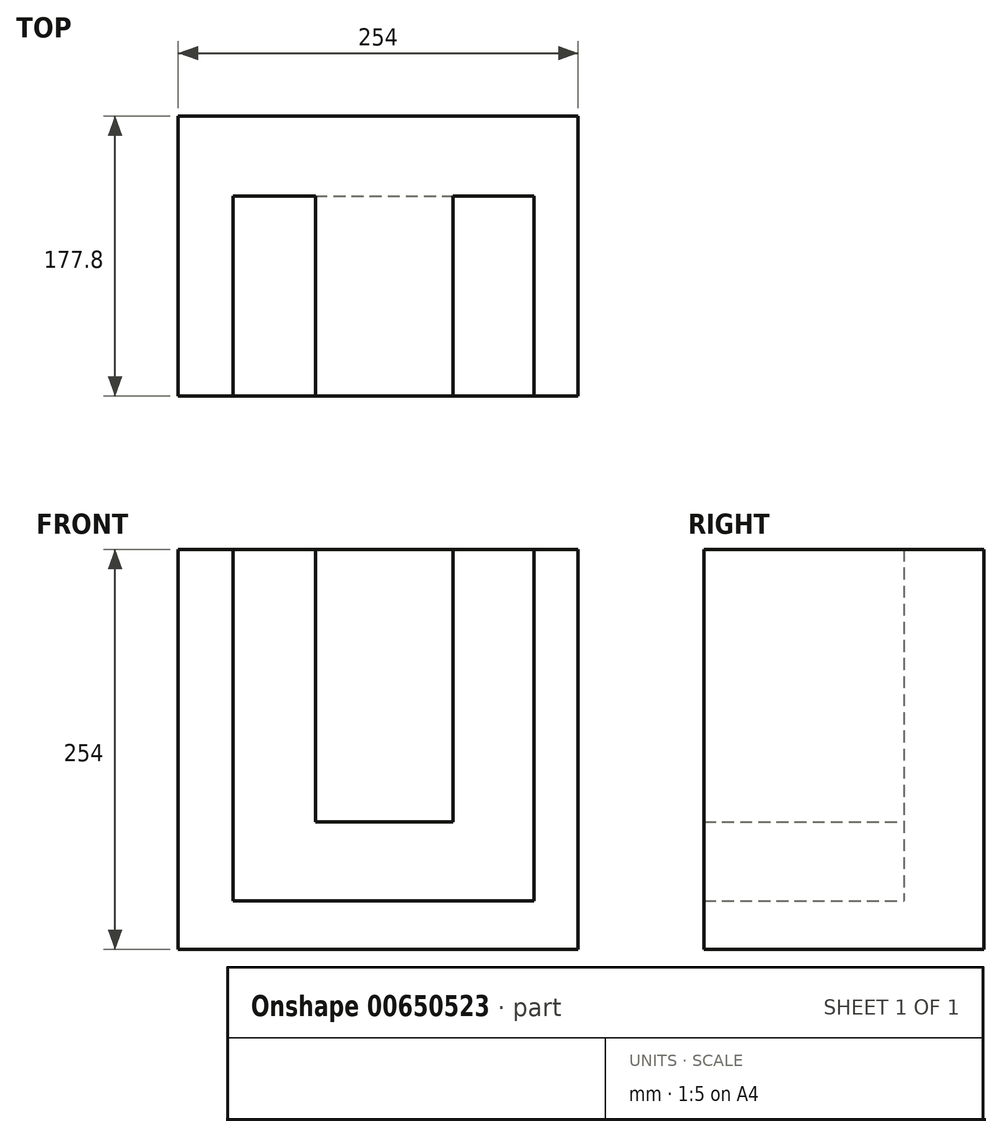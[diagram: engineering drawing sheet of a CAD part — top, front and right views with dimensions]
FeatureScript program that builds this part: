
annotation { "Feature Type Name" : "Feature", "Feature Type Description" : "" }
export const myFeature = defineFeature(function(context is Context, id is Id, definition is map)
    precondition{}
    {
        {
            var Q0;
            Q0=qCreatedBy(makeId("Front.planeOp"),FACE);
            var sketch = newSketch(context, id + "F0", { "sketchPlane" : qUnion([Q0])});
            skLineSegment(sketch, "E0.bottom", {"start": v(-59.5, 123.03) * mm, "end": v(194.5, 123.03) * mm});
            skLineSegment(sketch, "E0.top", {"start": v(-59.5, -130.97) * mm, "end": v(194.5, -130.97) * mm});
            skLineSegment(sketch, "E0.left", {"start": v(-59.5, 123.03) * mm, "end": v(-59.5, -130.97) * mm});
            skLineSegment(sketch, "E0.right", {"start": v(194.5, 123.03) * mm, "end": v(194.5, -130.97) * mm});
            skSolve(sketch);
        }
        {
            var Q0;
            Q0=makeQuery(id+"F0.imprint","IMPRINT",FACE,{"disambiguationData":[TD([[makeQuery(id+"F0.imprint","IMPRINT",EDGE,{"derivedFrom":sQuery(id+"F0.wireOp",EDGE,"E0.bottom")}),-1.0]])]});
            extrude(context, id + "F1", {"entities" : qUnion([Q0]), "depth" : 50.8 * mm, "offsetDistance" : 25.4 * mm});
        }
        {
            var Q0;
            Q0=makeQuery(id+"F1.opExtrude","CAP_FACE",FACE,{"disambiguationData":[OSD([sQuery(id+"F0.wireOp",EDGE,"E0.bottom"),sQuery(id+"F0.wireOp",EDGE,"E0.top"),sQuery(id+"F0.wireOp",EDGE,"E0.left"),sQuery(id+"F0.wireOp",EDGE,"E0.right")])],"isStart":false});
            var sketch = newSketch(context, id + "F2", { "sketchPlane" : qUnion([Q0])});
            skLineSegment(sketch, "E1.bottom", {"start": v(27.64, 123.03) * mm, "end": v(115, 123.03) * mm});
            skLineSegment(sketch, "E1.top", {"start": v(27.64, -49.92) * mm, "end": v(115, -49.92) * mm});
            skLineSegment(sketch, "E1.left", {"start": v(27.64, 123.03) * mm, "end": v(27.64, -49.92) * mm});
            skLineSegment(sketch, "E1.right", {"start": v(115, 123.03) * mm, "end": v(115, -49.92) * mm});
            skLineSegment(sketch, "E2.bottom", {"start": v(-24.78, 123.03) * mm, "end": v(166.34, 123.03) * mm});
            skLineSegment(sketch, "E2.top", {"start": v(-24.78, -100.15) * mm, "end": v(166.34, -100.15) * mm});
            skLineSegment(sketch, "E2.left", {"start": v(-24.78, 123.03) * mm, "end": v(-24.78, -100.15) * mm});
            skLineSegment(sketch, "E2.right", {"start": v(166.34, 123.03) * mm, "end": v(166.34, -100.15) * mm});
            skSolve(sketch);
        }
        {
            var Q0;
            Q0=makeQuery(id+"F2.imprint","IMPRINT",FACE,{"disambiguationData":[TD([[makeQuery(id+"F2.imprint","IMPRINT",EDGE,{"derivedFrom":sQuery(id+"F2.wireOp",EDGE,"E1.top")}),1.0]])]});
            var Q1;
            Q1=makeQuery(id+"F2.imprint","IMPRINT",FACE,{"disambiguationData":[TD([[makeQuery(id+"F2.imprint","IMPRINT",EDGE,{"derivedFrom":sQuery(id+"F2.wireOp",EDGE,"E2.top")}),-1.0]])]});
            extrude(context, id + "F3", {"entities" : qUnion([Q0, Q1]), "operationType" : NewBodyOperationType.ADD, "depth" : 127 * mm, "offsetDistance" : 25.4 * mm});
        }
    });
